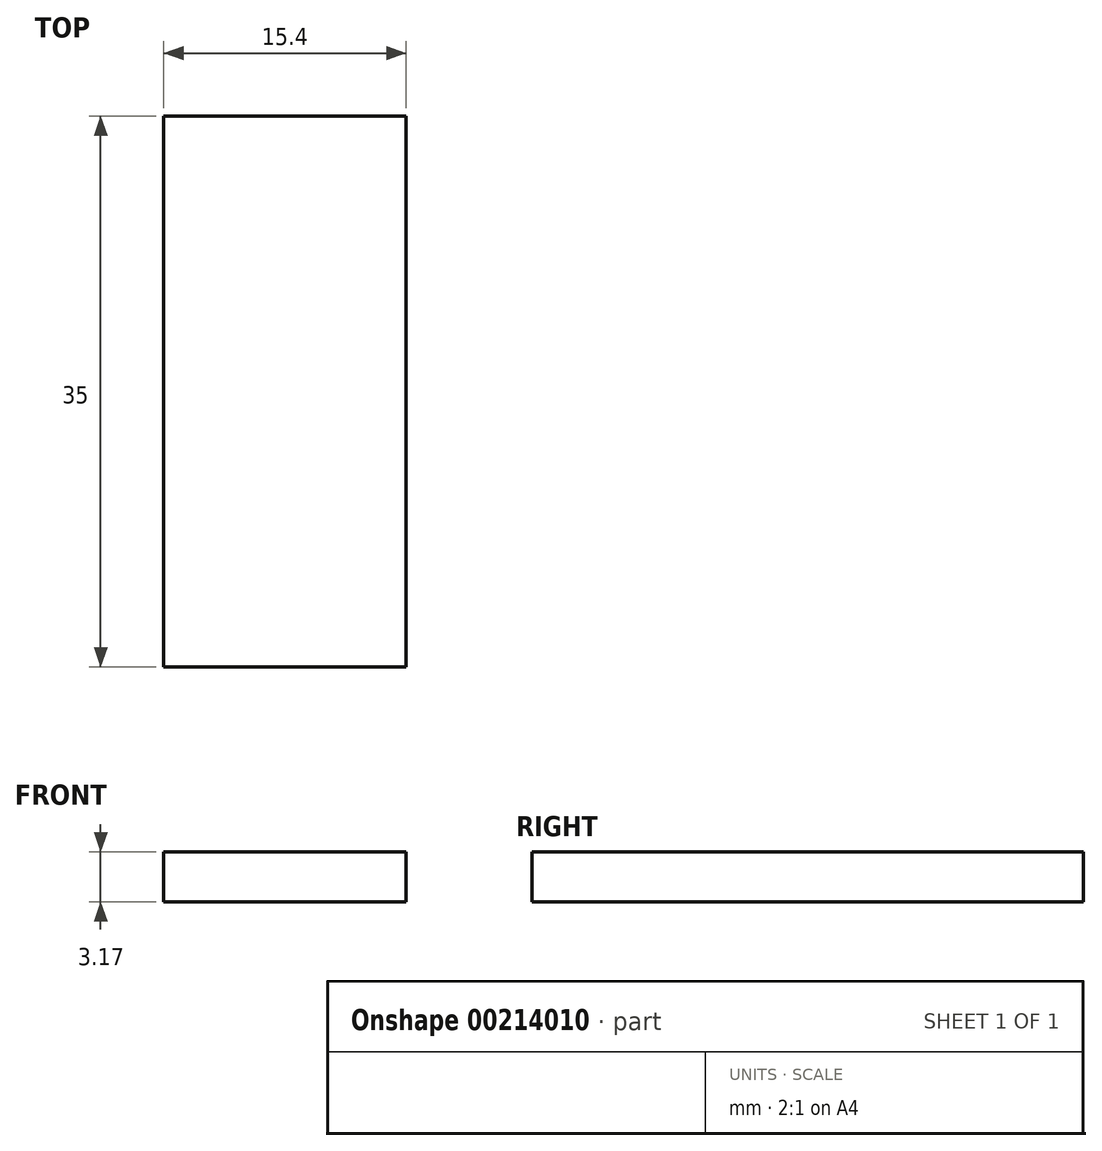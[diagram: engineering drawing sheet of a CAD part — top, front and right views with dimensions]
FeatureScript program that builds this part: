
annotation { "Feature Type Name" : "Feature", "Feature Type Description" : "" }
export const myFeature = defineFeature(function(context is Context, id is Id, definition is map)
    precondition{}
    {
        {
            var Q0;
            Q0=qCreatedBy(makeId("Top.planeOp"),FACE);
            var sketch = newSketch(context, id + "F0", { "sketchPlane" : qUnion([Q0])});
            skLineSegment(sketch, "E0.bottom", {"start": v(7.7, 17.5) * mm, "end": v(-7.7, 17.5) * mm});
            skLineSegment(sketch, "E0.top", {"start": v(7.7, -17.5) * mm, "end": v(-7.7, -17.5) * mm});
            skLineSegment(sketch, "E0.left", {"start": v(7.7, 17.5) * mm, "end": v(7.7, -17.5) * mm});
            skLineSegment(sketch, "E0.right", {"start": v(-7.7, 17.5) * mm, "end": v(-7.7, -17.5) * mm});
            skPoint(sketch, "E0.middle", {"position": v(0, 0) * mm});
            skSolve(sketch);
        }
        {
            var Q0;
            Q0 = qSketchRegion(id + "F0", true);
            extrude(context, id + "F1", {"entities" : qUnion([Q0]), "depth" : 3.17 * mm});
        }
    });
